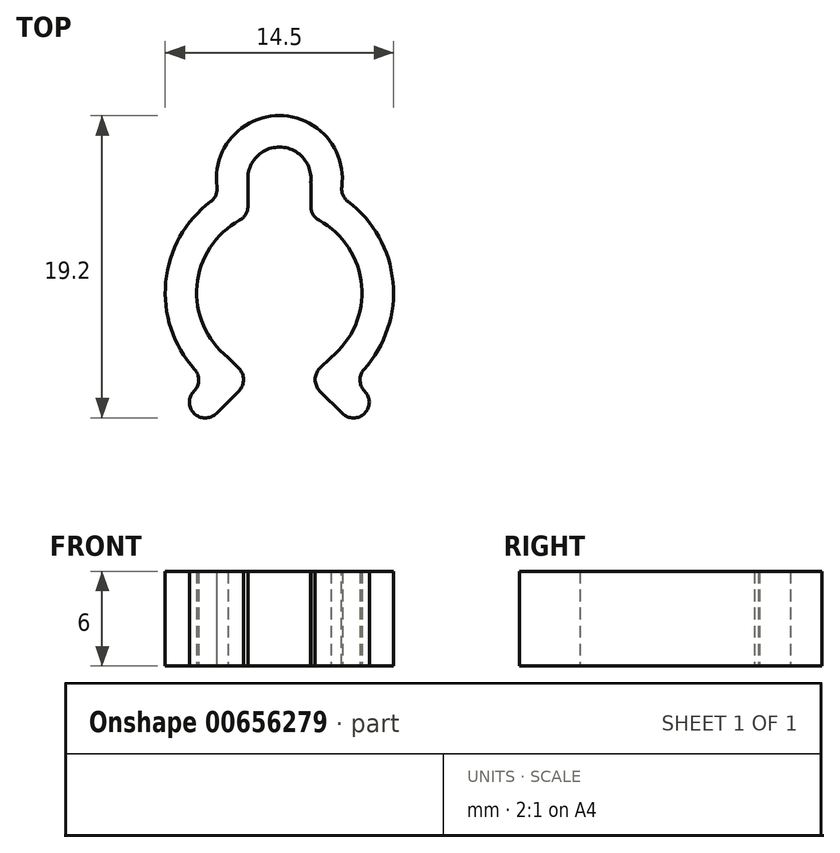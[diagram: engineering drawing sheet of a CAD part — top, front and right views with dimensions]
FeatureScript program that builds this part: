
annotation { "Feature Type Name" : "Feature", "Feature Type Description" : "" }
export const myFeature = defineFeature(function(context is Context, id is Id, definition is map)
    precondition{}
    {
        {
            var Q0;
            Q0=qCreatedBy(makeId("Top.planeOp"),FACE);
            var sketch = newSketch(context, id + "F0", { "sketchPlane" : qUnion([Q0])});
            skLineSegment(sketch, "E0", {"start": v(-11.9, 11.9) * mm, "end": v(0, 0) * mm, "construction": true});
            skLineSegment(sketch, "E1", {"start": v(0, 0) * mm, "end": v(12.42, 12.42) * mm, "construction": true});
            skLineSegment(sketch, "E2", {"start": v(-6.12, -6.12) * mm, "end": v(-4.7, -4.7) * mm, "construction": true});
            skLineSegment(sketch, "E3", {"start": v(-0.42, 0.42) * mm, "end": v(3.27, -3.27) * mm, "construction": true});
            skLineSegment(sketch, "E4.top", {"start": v(-6.12, -6.12) * mm, "end": v(-4.71, -7.54) * mm});
            skLineSegment(sketch, "E4.left", {"start": v(-4.7, -4.7) * mm, "end": v(-6.12, -6.12) * mm});
            skLineSegment(sketch, "E4.right", {"start": v(-1.86, -4.69) * mm, "end": v(-4.71, -7.54) * mm});
            skLineSegment(sketch, "E5.top", {"start": v(4.71, -7.54) * mm, "end": v(6.12, -6.12) * mm});
            skLineSegment(sketch, "E5.left", {"start": v(1.86, -4.69) * mm, "end": v(4.71, -7.54) * mm});
            skLineSegment(sketch, "E5.right", {"start": v(4.7, -4.7) * mm, "end": v(6.12, -6.12) * mm});
            skLineSegment(sketch, "E6.trimOffspring", {"start": v(-3.27, -3.27) * mm, "end": v(0, 0) * mm, "construction": true});
            skLineSegment(sketch, "E7.trimOffspring", {"start": v(4.7, -4.7) * mm, "end": v(6.12, -6.12) * mm, "construction": true});
            skArc(sketch, "E8", {"start": v(4.7, -4.7) * mm, "mid": v(7.23, 1.36) * mm, "end": v(3.84, 6.98) * mm});
            skArc(sketch, "E9", {"start": v(3.27, -3.27) * mm, "mid": v(5.2, 1.57) * mm, "end": v(2, 5.69) * mm});
            skLineSegment(sketch, "E10", {"start": v(-8.97, -7.54) * mm, "end": v(9.72, -7.54) * mm, "construction": true});
            skArc(sketch, "E11", {"start": v(3.84, 6.98) * mm, "mid": v(0, 12.08) * mm, "end": v(-3.84, 6.98) * mm});
            skArc(sketch, "E12", {"start": v(1.98, 7.8) * mm, "mid": v(0, 10.08) * mm, "end": v(-1.98, 7.8) * mm});
            skLineSegment(sketch, "E13.left", {"start": v(-2, 8.1) * mm, "end": v(-2, 5.69) * mm});
            skLineSegment(sketch, "E13.right", {"start": v(2, 8.1) * mm, "end": v(2, 5.69) * mm});
            skArc(sketch, "E14.trimOffspring", {"start": v(-2, 5.69) * mm, "mid": v(-5.2, 1.57) * mm, "end": v(-3.27, -3.27) * mm});
            skArc(sketch, "E15.trimOffspring", {"start": v(-1.98, 7.8) * mm, "mid": v(-2, 7.8) * mm, "end": v(-2, 7.8) * mm});
            skArc(sketch, "E16.trimOffspring", {"start": v(2, 7.8) * mm, "mid": v(2, 7.8) * mm, "end": v(1.98, 7.8) * mm});
            skArc(sketch, "E17.trimOffspring", {"start": v(-3.84, 6.98) * mm, "mid": v(-7.23, 1.36) * mm, "end": v(-4.7, -4.7) * mm});
            skCircle(sketch, "E18", {"center": v(0, 0.83) * mm, "radius": 5.25 * mm, "construction": true});
            skLineSegment(sketch, "E19", {"start": v(-3.27, -3.27) * mm, "end": v(-1.86, -4.69) * mm});
            skLineSegment(sketch, "E20", {"start": v(1.86, -4.69) * mm, "end": v(3.27, -3.27) * mm});
            skSolve(sketch);
        }
        {
            var Q0;
            Q0=qSketchRegion(id+"F0",true);
            extrude(context, id + "F1", {"entities" : qUnion([Q0]), "depth" : 6 * mm});
        }
        {
            var Q0;
            Q0=makeQuery(id+"F1.opExtrude","SWEPT_EDGE",EDGE,{"disambiguationData":[OSD([sQuery(id+"F0.wireOp",EDGE,"E4.top"),sQuery(id+"F0.wireOp",EDGE,"E4.right")])]});
            var Q1;
            Q1=makeQuery(id+"F1.opExtrude","SWEPT_EDGE",EDGE,{"disambiguationData":[OSD([sQuery(id+"F0.wireOp",EDGE,"E4.top"),sQuery(id+"F0.wireOp",EDGE,"E4.left")])]});
            var Q2;
            Q2=makeQuery(id+"F1.opExtrude","SWEPT_EDGE",EDGE,{"disambiguationData":[OSD([sQuery(id+"F0.wireOp",EDGE,"E5.top"),sQuery(id+"F0.wireOp",EDGE,"E5.left")])]});
            var Q3;
            Q3=makeQuery(id+"F1.opExtrude","SWEPT_EDGE",EDGE,{"disambiguationData":[OSD([sQuery(id+"F0.wireOp",EDGE,"E5.top"),sQuery(id+"F0.wireOp",EDGE,"E5.right")])]});
            var Q4;
            Q4=makeQuery(id+"F1.opExtrude","SWEPT_EDGE",EDGE,{"disambiguationData":[OSD([sQuery(id+"F0.wireOp",EDGE,"E5.bottom"),sQuery(id+"F0.wireOp",EDGE,"E5.left")])]});
            var Q5;
            Q5=makeQuery(id+"F1.opExtrude","SWEPT_EDGE",EDGE,{"disambiguationData":[OSD([sQuery(id+"F0.wireOp",EDGE,"E4.bottom"),sQuery(id+"F0.wireOp",EDGE,"E4.right")])]});
            var Q6;
            Q6=makeQuery(id+"F1.opExtrude","SWEPT_EDGE",EDGE,{"disambiguationData":[OSD([sQuery(id+"F0.wireOp",EDGE,"9W6XZ9US-gSVS-xIni-lCYk-6tlzBt2sRI0z"),sQuery(id+"F0.wireOp",EDGE,"bda73a1b-fc0e-4310-a31f-7d99da41a68f.trimOffspring")])]});
            var Q7;
            Q7=makeQuery(id+"F1.opExtrude","SWEPT_EDGE",EDGE,{"disambiguationData":[OSD([sQuery(id+"F0.wireOp",EDGE,"KrR6TGkJ-JJeF-ongJ-F6Q1-ZecX7Vko4zB8"),sQuery(id+"F0.wireOp",EDGE,"3bbdd5ad-7d6b-4629-afe7-84286cd13960.trimOffspring")])]});
            var Q8;
            Q8=makeQuery(id+"F1.opExtrude","SWEPT_EDGE",EDGE,{"disambiguationData":[OSD([sQuery(id+"F0.wireOp",EDGE,"9W6XZ9US-gSVS-xIni-lCYk-6tlzBt2sRI0z"),sQuery(id+"F0.wireOp",EDGE,"95556971-2a64-47c8-a68d-6902c3af31c1.trimOffspring")])]});
            var Q9;
            Q9=makeQuery(id+"F1.opExtrude","SWEPT_EDGE",EDGE,{"disambiguationData":[OSD([sQuery(id+"F0.wireOp",EDGE,"KrR6TGkJ-JJeF-ongJ-F6Q1-ZecX7Vko4zB8"),sQuery(id+"F0.wireOp",EDGE,"95556971-2a64-47c8-a68d-6902c3af31c1.trimOffspring")])]});
            var Q10;
            Q10=makeQuery(id+"F1.opExtrude","SWEPT_EDGE",EDGE,{"disambiguationData":[OSD([sQuery(id+"F0.wireOp",EDGE,"AmPDn02N-wigu-wboo-nWvt-QhuOuKc6RhIC"),sQuery(id+"F0.wireOp",EDGE,"9bdbd6fb-892b-475b-b5d3-7baefb43ca5d.trimOffspring")])]});
            var Q11;
            Q11=makeQuery(id+"F1.opExtrude","SWEPT_EDGE",EDGE,{"disambiguationData":[OSD([sQuery(id+"F0.wireOp",EDGE,"aYfYm9uv-R0JL-swxI-bSqR-EboSUTluJaZa"),sQuery(id+"F0.wireOp",EDGE,"9bdbd6fb-892b-475b-b5d3-7baefb43ca5d.trimOffspring")])]});
            var Q12;
            Q12=makeQuery(id+"F1.opExtrude","SWEPT_EDGE",EDGE,{"disambiguationData":[OSD([sQuery(id+"F0.wireOp",EDGE,"TLjRqDxk-6mDp-7GRj-fjIY-TCOmEL0ilI2E"),sQuery(id+"F0.wireOp",EDGE,"fmtMBntk-y6TB-78qn-WZfk-syJzKedwu172")])]});
            var Q13;
            Q13=makeQuery(id+"F1.opExtrude","SWEPT_EDGE",EDGE,{"disambiguationData":[OSD([sQuery(id+"F0.wireOp",EDGE,"1l2sMWYM-ZpTZ-Tr11-wPrr-ifopXtd3ZZ9B"),sQuery(id+"F0.wireOp",EDGE,"d747fa4c-82df-41d5-9920-b1f4d2df55ee.trimOffspring")])]});
            var Q14;
            Q14=makeQuery(id+"F1.opExtrude","SWEPT_EDGE",EDGE,{"disambiguationData":[OSD([sQuery(id+"F0.wireOp",EDGE,"3bbdd5ad-7d6b-4629-afe7-84286cd13960.trimOffspring"),sQuery(id+"F0.wireOp",EDGE,"E4.left")])]});
            var Q15;
            Q15=makeQuery(id+"F1.opExtrude","SWEPT_EDGE",EDGE,{"disambiguationData":[OSD([sQuery(id+"F0.wireOp",EDGE,"E5.right"),sQuery(id+"F0.wireOp",EDGE,"bda73a1b-fc0e-4310-a31f-7d99da41a68f.trimOffspring")])]});
            var Q16;
            Q16=makeQuery(id+"F1.opExtrude","SWEPT_EDGE",EDGE,{"disambiguationData":[OSD([sQuery(id+"F0.wireOp",EDGE,"E9"),sQuery(id+"F0.wireOp",EDGE,"E13.right")])]});
            var Q17;
            Q17=makeQuery(id+"F1.opExtrude","SWEPT_EDGE",EDGE,{"disambiguationData":[OSD([sQuery(id+"F0.wireOp",EDGE,"E11"),sQuery(id+"F0.wireOp",EDGE,"E17.trimOffspring")])]});
            var Q18;
            Q18=makeQuery(id+"F1.opExtrude","SWEPT_EDGE",EDGE,{"disambiguationData":[OSD([sQuery(id+"F0.wireOp",EDGE,"E13.left"),sQuery(id+"F0.wireOp",EDGE,"E14.trimOffspring")])]});
            var Q19;
            Q19=makeQuery(id+"F1.opExtrude","SWEPT_EDGE",EDGE,{"disambiguationData":[OSD([sQuery(id+"F0.wireOp",EDGE,"E8"),sQuery(id+"F0.wireOp",EDGE,"E11")])]});
            fillet(context, id + "F2", {"entities" : qUnion([Q0, Q1, Q2, Q3, Q4, Q5, Q6, Q7, Q8, Q9, Q10, Q11, Q12, Q13, Q14, Q15, Q16, Q17, Q18, Q19]), "radius" : 1 * mm, "tangentPropagation" : true, "allowEdgeOverflow" : false});
        }
    });
